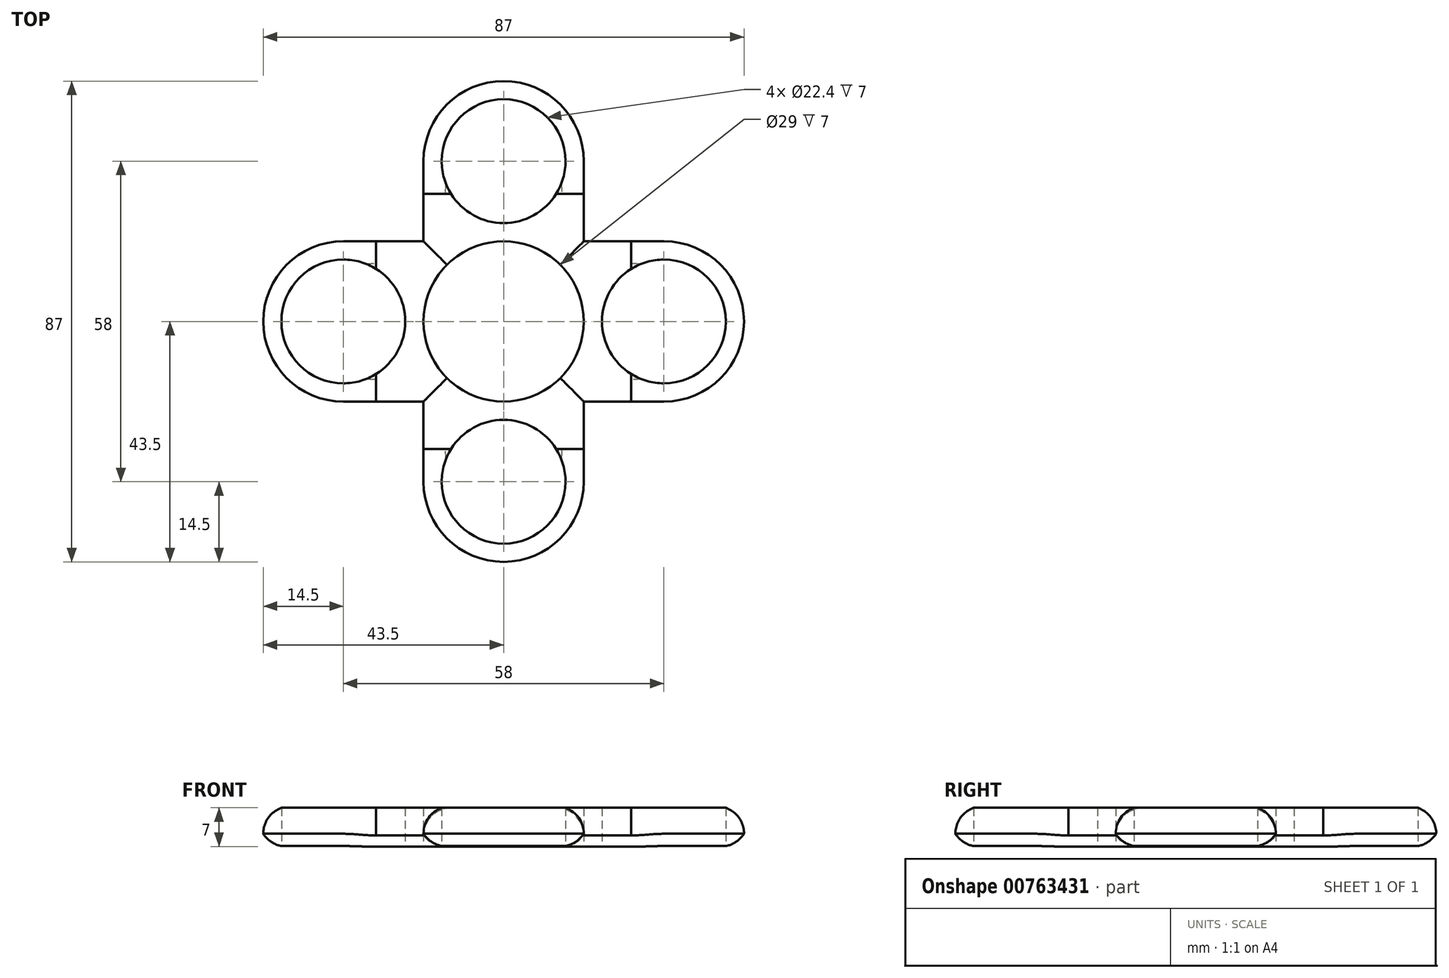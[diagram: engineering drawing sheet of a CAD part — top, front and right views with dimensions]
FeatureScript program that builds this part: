
annotation { "Feature Type Name" : "Feature", "Feature Type Description" : "" }
export const myFeature = defineFeature(function(context is Context, id is Id, definition is map)
    precondition{}
    {
        {
            var Q0;
            Q0=qCreatedBy(makeId("Top.planeOp"),FACE);
            var sketch = newSketch(context, id + "F0", { "sketchPlane" : qUnion([Q0])});
            skCircle(sketch, "E0", {"center": v(0, 0) * mm, "radius": 14.5 * mm});
            skCircle(sketch, "E1", {"center": v(0, 0) * mm, "radius": 11.2 * mm});
            skCircle(sketch, "E2", {"center": v(0, 29) * mm, "radius": 14.5 * mm});
            skCircle(sketch, "E3", {"center": v(0, 29) * mm, "radius": 11.2 * mm});
            skCircle(sketch, "E4.1.0", {"center": v(-29, 0) * mm, "radius": 11.2 * mm});
            skCircle(sketch, "E4.1.1", {"center": v(-29, 0) * mm, "radius": 14.5 * mm});
            skCircle(sketch, "E4.2.0", {"center": v(0, -29) * mm, "radius": 11.2 * mm});
            skCircle(sketch, "E4.2.1", {"center": v(0, -29) * mm, "radius": 14.5 * mm});
            skCircle(sketch, "E4.3.0", {"center": v(29, 0) * mm, "radius": 11.2 * mm});
            skCircle(sketch, "E4.3.1", {"center": v(29, 0) * mm, "radius": 14.5 * mm});
            skLineSegment(sketch, "E5", {"start": v(0, 14.5) * mm, "end": v(29, 14.5) * mm});
            skLineSegment(sketch, "E6", {"start": v(14.5, 0) * mm, "end": v(14.5, -29) * mm});
            skLineSegment(sketch, "E7", {"start": v(0, -14.5) * mm, "end": v(-29, -14.5) * mm});
            skLineSegment(sketch, "E8", {"start": v(-14.5, 0) * mm, "end": v(-14.5, 29) * mm});
            skLineSegment(sketch, "E9", {"start": v(14.5, 0) * mm, "end": v(14.5, 29) * mm});
            skLineSegment(sketch, "E10", {"start": v(0, 14.5) * mm, "end": v(-29, 14.5) * mm});
            skLineSegment(sketch, "E11", {"start": v(-14.5, 0) * mm, "end": v(-14.5, -29) * mm});
            skLineSegment(sketch, "E12", {"start": v(0, -14.5) * mm, "end": v(29, -14.5) * mm});
            skSolve(sketch);
        }
        {
            var Q0;
            Q0 = qSketchRegion(id + "F0", true);
            extrude(context, id + "F1", {"entities" : qUnion([Q0]), "depth" : 7 * mm, "offsetDistance" : 25 * mm});
        }
        {
            var Q0;
            Q0=makeQuery(id+"F1.opExtrude","CAP_EDGE",EDGE,{"disambiguationData":[OSD([sQuery(id+"F0.wireOp",EDGE,"E2")])],"isStart":false});
            var Q1;
            Q1=makeQuery(id+"F1.opExtrude","CAP_EDGE",EDGE,{"disambiguationData":[OSD([sQuery(id+"F0.wireOp",EDGE,"E4.3.1")])],"isStart":false});
            var Q2;
            Q2=makeQuery(id+"F1.opExtrude","CAP_EDGE",EDGE,{"disambiguationData":[OSD([sQuery(id+"F0.wireOp",EDGE,"E4.2.1")])],"isStart":false});
            var Q3;
            Q3=makeQuery(id+"F1.opExtrude","CAP_EDGE",EDGE,{"disambiguationData":[OSD([sQuery(id+"F0.wireOp",EDGE,"E4.1.1")])],"isStart":false});
            fillet(context, id + "F2", {"entities" : qUnion([Q0, Q1, Q2, Q3]), "radius" : 5 * mm, "tangentPropagation" : true, "allowEdgeOverflow" : false});
        }
        {
            var Q0;
            Q0=makeQuery(id+"F1.opExtrude","CAP_EDGE",EDGE,{"disambiguationData":[OSD([sQuery(id+"F0.wireOp",EDGE,"E2")])],"isStart":true});
            var Q1;
            Q1=makeQuery(id+"F1.opExtrude","CAP_EDGE",EDGE,{"disambiguationData":[OSD([sQuery(id+"F0.wireOp",EDGE,"E4.1.1")])],"isStart":true});
            var Q2;
            Q2=makeQuery(id+"F1.opExtrude","CAP_EDGE",EDGE,{"disambiguationData":[OSD([sQuery(id+"F0.wireOp",EDGE,"E4.2.1")])],"isStart":true});
            var Q3;
            Q3=makeQuery(id+"F1.opExtrude","CAP_EDGE",EDGE,{"disambiguationData":[OSD([sQuery(id+"F0.wireOp",EDGE,"E4.3.1")])],"isStart":true});
            fillet(context, id + "F3", {"entities" : qUnion([Q0, Q1, Q2, Q3]), "radius" : 5 * mm, "tangentPropagation" : true, "allowEdgeOverflow" : false});
        }
    });
